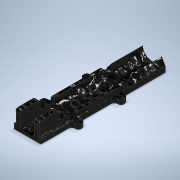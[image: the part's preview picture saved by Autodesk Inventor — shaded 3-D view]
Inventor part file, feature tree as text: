
AUTODESK INVENTOR PART (.ipt)
format: ipt  version: 2020 (Build 240168000, 168)  size: 793,600 bytes
history: native  units: mm
features: projected_geometry x24, extrude x16, sketch x16, fillet x9, hole x2, chamfer x2, plane x1, direct_edit x1, move_body x1
ambient origin geometry x8: Origin, YZ Plane, XZ Plane, XY Plane, X Axis, Y Axis, Z Axis, Center Point
bodies: Solid1 (feature_tree)
feature tree (72):
  extrude  "Extrusion1"  Depth=100.0mm
  plane  "Work Plane1"
  sketch  "Sketch2"  dims[d2=6.0mm d3=0.0mm d4=-7.0mm]
  extrude  "Extrusion2"  [1 undecoded]
  extrude  "Extrusion7"  Depth=21.5mm
  extrude  "Extrusion3"  Depth=12.5mm
  hole  "Hole1"  [1 undecoded]
  direct_edit  "Direct Edit1"
  extrude  "Extrusion4"  Depth=3.0mm
  extrude  "Extrusion5"  Depth=3.0mm
  extrude  "Extrusion6"  Depth=2.0mm
  hole  "Hole2"  [1 undecoded]
  extrude  "Extrusion8"  Depth=31.0mm TaperAngle=0.0deg
  fillet  "Fillet1"  Radius=10.5mm
  fillet  "Fillet2"  Radius=31.0mm
  fillet  "Fillet3"  Radius=2.95mm
  chamfer  "Chamfer1"  Distance=14.0mm
  chamfer  "Chamfer2"  Distance=7.0mm
  fillet  "Fillet4"  Radius=7.0mm
  extrude  "Extrusion9"  Depth=2.0mm TaperAngle=0.0deg
  fillet  "Fillet5"  Radius=3.5mm
  extrude  "Extrusion10"  Depth=2.0mm
  extrude  "Extrusion11"  Depth=2.0mm
  extrude  "Extrusion12"  Depth=2.0mm
  extrude  "Extrusion13"  Depth=31.0mm
  fillet  "Fillet6"  Radius=38.0mm
  extrude  "Extrusion14"  Depth=2.0mm
  extrude  "Extrusion15"  Depth=2.0mm TaperAngle=0.0deg
  fillet  "Fillet7"  Radius=55.0mm
  fillet  "Fillet8"  Radius=176.0mm
  extrude  "Extrusion16"  Depth=2.0mm
  fillet  "Fillet9"  Radius=85.25mm
  sketch  "Sketch1"  dims[d0=29.0mm d1=100.0mm]
  projected_geometry  "Projected Loop1"
  sketch  "Sketch3"  dims[d5=12.5mm d6=21.5mm]
  projected_geometry  "Projected Loop2"
  sketch  "Sketch4"  dims[d7=51.8mm d8=0.0mm d9=12.5mm]
  projected_geometry  "Projected Loop3"
  sketch  "Sketch5"  dims[d10=20.0mm d11=34.0mm d12=0.0mm]
  projected_geometry  "Projected Loop4"
  projected_geometry  "Projected Loop5"
  sketch  "Sketch7"  dims[d13=3.0mm d14=5.0mm]
  projected_geometry  "Projected Loop6"
  sketch  "Sketch8"  dims[d15=3.0mm d16=5.0mm]
  projected_geometry  "Projected Loop7"
  sketch  "Sketch9"  dims[d17=3.1mm d18=6.0mm d19=5.5mm d20=2.0mm d21=90.0deg d22=6.0mm d23=0.0mm d24=5.0mm]
  projected_geometry  "Projected Loop8"
  sketch  "Sketch10"  dims[d25=63.0mm d26=5.0mm]
  projected_geometry  "Projected Loop9"
  sketch  "Sketch11"  dims[d27=63.0mm d28=0.0mm d29=0.0mm d30=31.0mm d31=10.5mm d32=31.0mm d33=2.95mm d34=0.0mm]
  projected_geometry  "Projected Loop10"
  sketch  "Sketch12"  dims[d35=5.0mm]
  projected_geometry  "Projected Loop11"
  projected_geometry  "Projected Loop12"
  projected_geometry  "Projected Loop13"
  sketch  "Sketch14"  dims[d36=20.0mm]
  sketch  "Sketch16"  dims[d37=5.0mm]
  projected_geometry  "Projected Loop22"
  sketch  "Sketch17"  dims[d38=20.0mm d39=14.0mm d40=0.0mm]
  projected_geometry  "Projected Loop23"
  projected_geometry  "Projected Loop24"
  projected_geometry  "Projected Loop25"
  sketch  "Sketch18"  dims[d41=7.0mm]
  projected_geometry  "Projected Loop26"
  projected_geometry  "Projected Loop27"
  projected_geometry  "Projected Loop28"
  projected_geometry  "Projected Loop29"
  projected_geometry  "Projected Loop30"
  sketch  "Sketch19"  dims[d42=7.0mm d43=7.0mm d44=7.0mm d45=6.0mm d46=0.0mm d47=3.5mm d48=3.5mm d49=3.5mm d50=3.5mm d51=3.1mm d52=6.0mm d53=5.5mm d54=2.0mm d55=90.0deg d56=6.0mm d57=0.0mm d58=31.0mm d59=38.0mm d60=34.0mm d61=6.75mm d62=0.0mm d63=55.0mm d64=176.0mm d65=152.0mm d66=85.25mm d67=0.0mm d68=1.0mm d69=3.0mm d70=3.0mm d71=3.0mm d72=1.0mm d73=4.5mm d74=6.0mm d75=45.0deg d76=4.5mm d77=6.0mm d78=45.0deg d79=1.0mm d80=1.45mm d81=0.0mm d82=3.0mm d83=1.0mm d84=6.1mm d85=27.2mm d87=14.5mm d88=53.8mm d89=0.1mm d90=0.1mm d91=5.0mm d92=0.0mm d93=5.0mm d94=53.75mm d95=0.0mm d96=0.0mm d98=15.0mm d99=0.0mm d100=17.25mm d101=0.0mm d102=2.0mm d103=0.15mm d104=0.15mm d105=0.15mm d106=0.15mm d107=0.0mm d108=17.25mm d109=0.0mm d110=8.25mm d111=0.0mm d112=2.0mm d113=0.25mm d114=1.0mm d115=0.0mm d116=2.0mm d117=0.872665mm d118=0.5mm d119=0.872665mm]
  projected_geometry  "Projected Loop31"
  projected_geometry  "Projected Loop32"
  move_body  "Move1"
note: 3 required parameter values undecoded (feature->parameter linkage not recoverable at this tier; creation-order binding heuristic only, values carry confidence <= 0.55)
